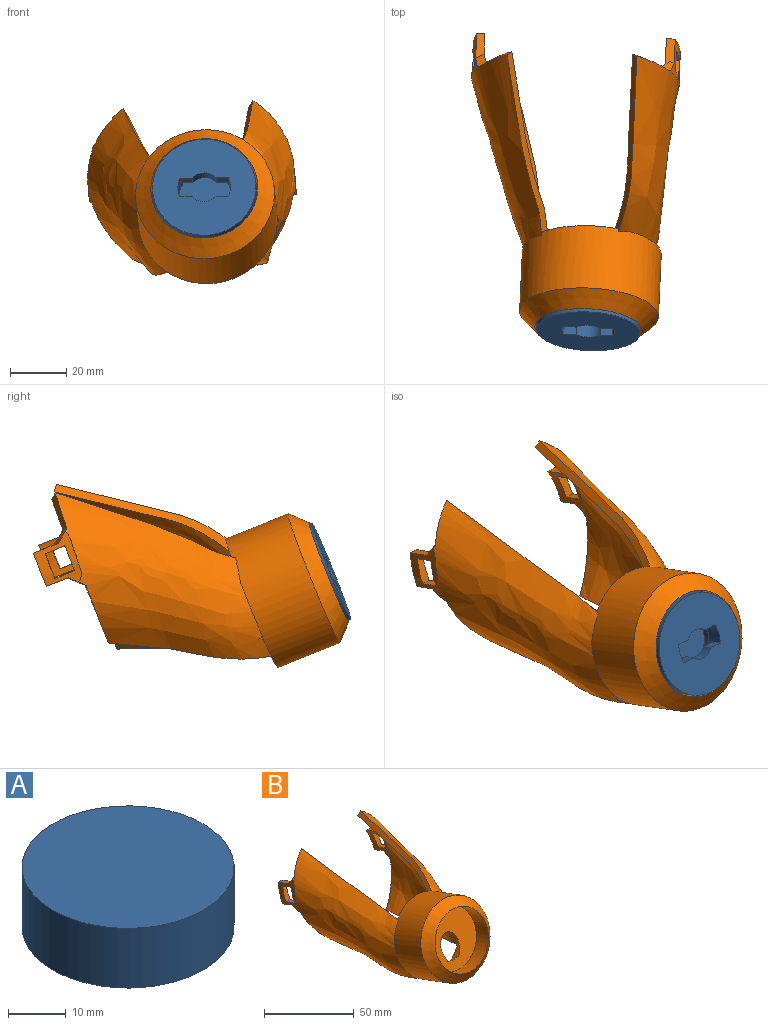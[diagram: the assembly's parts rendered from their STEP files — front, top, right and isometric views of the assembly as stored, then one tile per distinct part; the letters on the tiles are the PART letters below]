
ASSEMBLY  parts=2 mates=1
PART A: 17 faces, bbox 36.8x36.8x12.7 mm
  f0: cylinder r=5.52mm len=8.46mm, axis (0,0,1), area 42.8mm2, adj f2,f8,f12,f16
  f1: cylinder r=5.52mm len=8.46mm, axis (0,0,1), area 42.8mm2, adj f3,f8,f11,f14
  f2: plane 17.26x5.78mm, normal (0,0,1), area 60.6mm2, adj f0,f4,f12,f16
  f3: plane 17.26x5.78mm, normal (0,0,1), area 60.6mm2, adj f1,f4,f11,f14
  f4: cylinder r=9.33mm len=18.67mm, axis (0,0,1), area 232.9mm2, adj f2,f3,f5,f9,f11,f12,f13,f14
  f5: plane 18.67x18.67mm, normal (0,0,-1), area 273.7mm2, adj f4
  f6: plane 36.83x36.83mm, normal (0,0,1), area 1065.4mm2, adj f7
  f7: cylinder r=18.41mm len=36.83mm, axis (0,0,1), area 1469.5mm2, adj f6,f8
  f8: plane 36.83x36.83mm, normal (0,0,-1), area 911.8mm2, adj f0,f1,f7,f10,f11,f12,f14,f15
  f9: plane 7.11x0.77mm, normal (0,0,-1), area 0.5mm2, adj f4,f10,f11,f12
  f10: cylinder r=9.4mm len=7.11mm, axis (0,0,-1), area 46.3mm2, adj f8,f9,f11,f12
  f11: plane 6.35x4.47mm, normal (0,1,0), area 20mm2, adj f1,f3,f4,f8,f9,f10
  f12: plane 6.35x4.47mm, normal (0,-1,0), area 20mm2, adj f0,f2,f4,f8,f9,f10
  f13: plane 7.11x0.77mm, normal (0,0,-1), area 0.5mm2, adj f4,f14,f15,f16
  f14: plane 6.35x4.47mm, normal (0,1,0), area 20mm2, adj f1,f3,f4,f8,f13,f15
  f15: cylinder r=9.4mm len=7.11mm, axis (0,0,-1), area 46.3mm2, adj f8,f13,f14,f16
  f16: plane 6.35x4.47mm, normal (0,-1,0), area 20mm2, adj f0,f2,f4,f8,f13,f15
PART B: 55 faces, bbox 87.2x119.8x71.6 mm
  f0: extruded ~22.52x20.09mm, area 125.4mm2, adj f1,f45,f46,f47,f48,f49,f50,f51
  f1: plane 8.15x4.35mm, normal (-0.04,-0.93,0.37), area 26.4mm2, adj f0,f2,f45,f47
  f2: extruded ~19.07x18.06mm, area 105.7mm2, adj f1,f3,f44,f45,f46,f47,f49,f50
  f3: bspline ~82.22x56.39mm, area 2886.9mm2, adj f2,f4,f36,f37,f38,f39,f40,f41
  f4: revolved ~39.76x36.2mm, area 1707.4mm2, adj f3,f5,f30,f31,f32,f33,f34,f35
  f5: plane 30.84x25.15mm, normal (0.04,0.93,-0.37), area 97mm2, adj f4,f6,f28,f29,f30,f41,f43
  f6: cylinder r=24.72mm len=54.78mm, axis (-0.04,-0.93,0.37), area 3698.7mm2, adj f5,f7,f24,f25,f26,f28,f32,f33
  f7: bspline ~58.96x15.42mm, area 182.4mm2, adj f6,f8,f25,f31,f32,f35
  f8: bspline ~21.11x16.43mm, area 80.2mm2, adj f7,f9,f31,f32
  f9: bspline ~7.03x5.78mm, area 22.1mm2, adj f8,f10,f20,f21,f31,f32
  f10: extruded ~22.21x19.03mm, area 106.5mm2, adj f9,f11,f12,f13,f14,f15,f16,f17
  f11: plane 9.31x4.17mm, normal (-0.04,-0.93,0.37), area 27.6mm2, adj f10,f12,f14,f21
  f12: plane 7.18x3.14mm, normal (0,-0.37,-0.93), area 21.5mm2, adj f10,f11,f13,f21
  f13: plane 9.31x4.17mm, normal (0.04,0.93,-0.37), area 27.6mm2, adj f10,f12,f14,f21
  f14: plane 7.19x3.44mm, normal (0,0.37,0.93), area 23.8mm2, adj f10,f11,f13,f21
  f15: plane 11.85x4.81mm, normal (0.04,0.93,-0.37), area 37.2mm2, adj f10,f19,f20,f21
  f16: bspline ~11.7x4.88mm, area 0mm2, adj f10,f31
  f17: bspline ~7.55x6.1mm, area 21.6mm2, adj f10,f18,f19,f21,f31,f32
  f18: bspline ~19.47x13.72mm, area 49.6mm2, adj f17,f28,f31,f32
  f19: plane 8.92x3.6mm, normal (0,0.37,0.93), area 25.6mm2, adj f10,f15,f17,f21
  f20: plane 7.78x3.51mm, normal (0,-0.37,-0.93), area 25.2mm2, adj f9,f10,f15,f21
  f21: extruded ~22.76x20.08mm, area 119mm2, adj f9,f11,f12,f13,f14,f15,f17,f19
  f22: bspline ~25.12x9.56mm, area 0mm2, adj f21,f32
  f23: bspline ~12.37x5.12mm, area 0mm2, adj f21,f32
  f24: plane 31.86x13.1mm, normal (0.04,0.93,-0.37), area 87.4mm2, adj f6,f53
  f25: plane 34.49x13.51mm, normal (0.04,0.93,-0.37), area 83.3mm2, adj f6,f7,f35,f37,f38
  f26: cone r=17.1mm half-angle=45deg, axis (0.04,0.93,-0.37), area 1103.2mm2, adj f6,f27
  f27: cylinder r=19.05mm len=39.37mm, axis (0.04,0.93,-0.37), area 1287mm2, adj f26,f34
  f28: bspline ~65.33x25.44mm, area 219.8mm2, adj f5,f6,f18,f30,f31,f32
  f29: sphere r=22.23mm, area 188.1mm2, adj f5,f43
  f30: bspline ~21.51x8.62mm, area 10.4mm2, adj f4,f5,f28,f31
  f31: bspline ~82.72x56.66mm, area 2686.5mm2, adj f4,f7,f8,f9,f10,f16,f17,f18
  f32: offset ~88.06x62.66mm, area 3121mm2, adj f4,f6,f7,f8,f9,f17,f18,f21
  f33: plane 26.21x11.02mm, normal (0.04,0.93,-0.37), area 25.3mm2, adj f4,f6,f32,f35
  f34: plane 39.84x37.14mm, normal (-0.04,-0.93,0.37), area 965.6mm2, adj f4,f27,f35
  f35: sphere r=22.23mm, area 831.4mm2, adj f4,f7,f25,f31,f32,f33,f34
  f36: sphere r=22.23mm, area 2mm2, adj f3,f4,f37
  f37: bspline ~7.24x3.87mm, area 1.9mm2, adj f3,f25,f36,f38
  f38: bspline ~55.34x6.14mm, area 174mm2, adj f3,f6,f25,f37,f39,f53
  f39: bspline ~25.75x15.21mm, area 92.8mm2, adj f3,f38,f52,f53
  f40: bspline ~19.88x15.4mm, area 52.9mm2, adj f3,f41,f48,f53
  f41: bspline ~65.32x24.57mm, area 212.5mm2, adj f3,f5,f6,f40,f42,f53
  f42: sphere r=22.23mm, area 0mm2, adj f3,f41,f43
  f43: revolved ~21.18x10.19mm, area 13.6mm2, adj f3,f4,f5,f29,f42
  f44: bspline ~5.12x2.1mm, area 0mm2, adj f2,f3
  f45: plane 7.19x3.43mm, normal (0,-0.37,-0.93), area 23.7mm2, adj f0,f1,f2,f46
  f46: plane 8.15x4.35mm, normal (0.04,0.93,-0.37), area 26.4mm2, adj f0,f2,f45,f47
  f47: plane 7.19x3.41mm, normal (0,0.37,0.93), area 23.5mm2, adj f0,f1,f2,f46
  f48: bspline ~5.99x5.39mm, area 18.1mm2, adj f0,f3,f40,f49,f53
  f49: plane 11.78x4.73mm, normal (0,0.37,0.93), area 30.9mm2, adj f0,f2,f3,f48,f50
  f50: plane 11.81x4.97mm, normal (0.04,0.93,-0.37), area 39.1mm2, adj f0,f2,f49,f51
  f51: plane 7.77x3.45mm, normal (0,-0.37,-0.93), area 24.9mm2, adj f0,f2,f50,f52
  f52: bspline ~7.2x5.43mm, area 22.1mm2, adj f0,f2,f3,f39,f51,f53
  f53: offset ~85.85x61.77mm, area 3176.2mm2, adj f0,f6,f24,f38,f39,f40,f41,f48
  f54: bspline ~12.71x5.5mm, area 0mm2, adj f0,f53
PLACE A rot(axis=(-1,0.01,-0.02),111.9deg) t=(71.6,79.12,49.68)mm
PLACE B rot(axis=(0.13,0.85,0.51),0deg) t=(-144.48,-90.64,-123.17)mm
MATE fastened B.f6 <-> A.f0  axis (0.04,0.93,-0.37) through (71.89,85.42,47.15)mm
